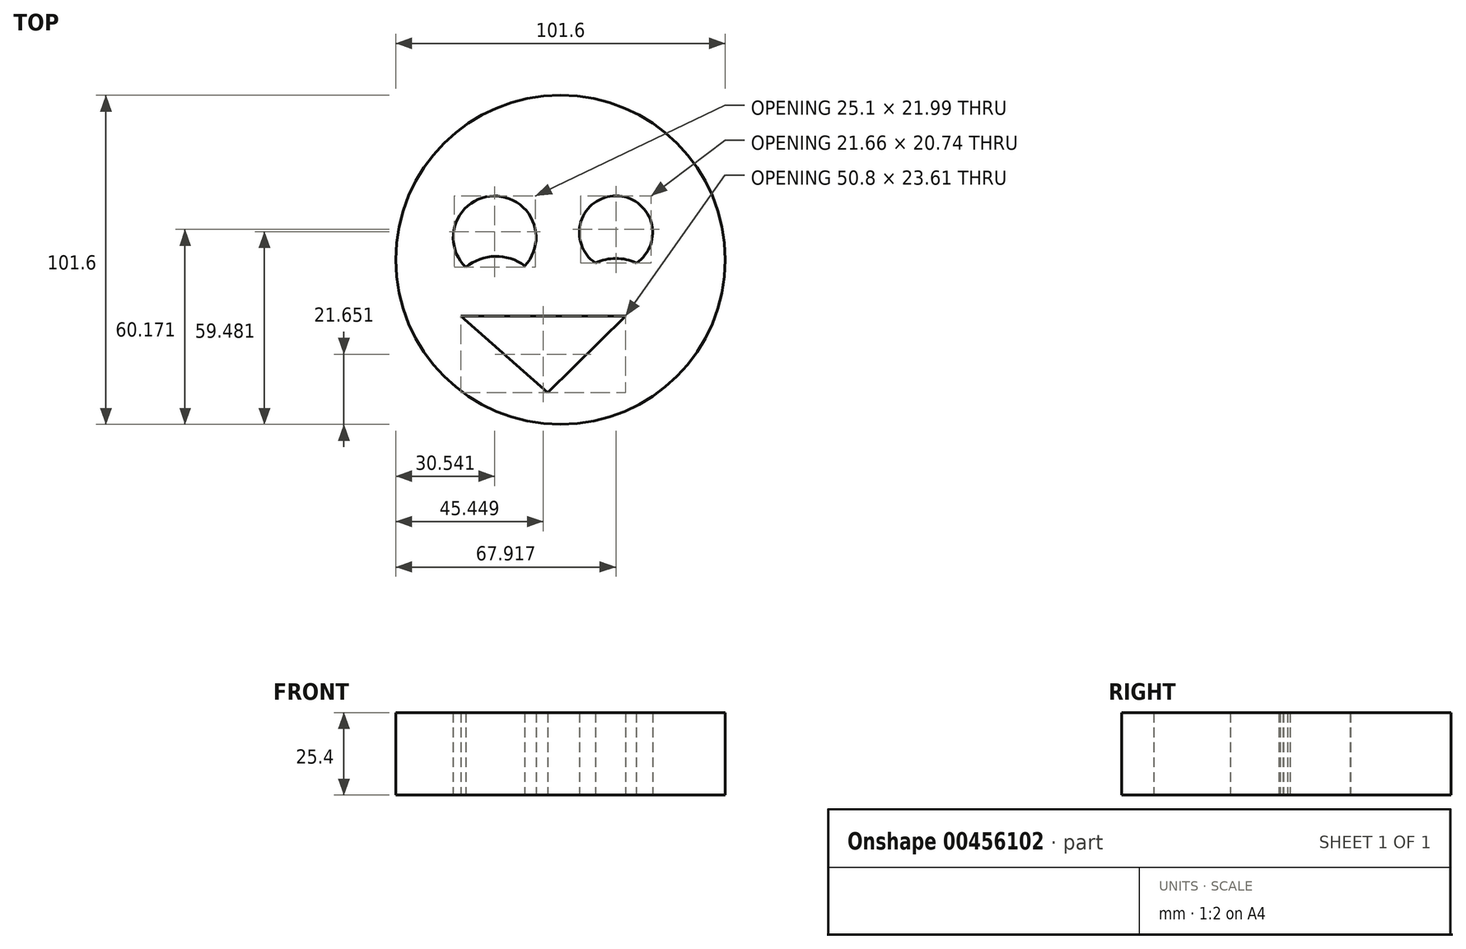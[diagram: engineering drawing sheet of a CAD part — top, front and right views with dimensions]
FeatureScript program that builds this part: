
annotation { "Feature Type Name" : "Feature", "Feature Type Description" : "" }
export const myFeature = defineFeature(function(context is Context, id is Id, definition is map)
    precondition{}
    {
        {
            var Q0;
            Q0=qCreatedBy(makeId("Top.planeOp"),FACE);
            var sketch = newSketch(context, id + "F0", { "sketchPlane" : qUnion([Q0])});
            skCircle(sketch, "E0", {"center": v(0, 0) * mm, "radius": 50.8 * mm});
            skLineSegment(sketch, "E1", {"start": v(-30.75, -17.34) * mm, "end": v(20.05, -17.34) * mm});
            skLineSegment(sketch, "E2", {"start": v(20.05, -17.34) * mm, "end": v(-3.93, -40.95) * mm});
            skLineSegment(sketch, "E3", {"start": v(-3.93, -40.95) * mm, "end": v(-30.75, -17.34) * mm});
            skArc(sketch, "E4", {"start": v(-8.6, -4.23) * mm, "mid": v(-20.04, 1.07) * mm, "end": v(-31.33, -4.52) * mm});
            skArc(sketch, "E5", {"start": v(26.67, -3.06) * mm, "mid": v(17.05, 0.41) * mm, "end": v(7.43, -3.06) * mm});
            skArc(sketch, "E6", {"start": v(-11.02, -1.9) * mm, "mid": v(-20.6, 19.68) * mm, "end": v(-29.2, -2.32) * mm});
            skArc(sketch, "E7", {"start": v(23.4, -1) * mm, "mid": v(17.14, 19.74) * mm, "end": v(10.76, -0.97) * mm});
            skSolve(sketch);
        }
        {
            var Q0;
            Q0=makeQuery(id+"F0.imprint","IMPRINT",FACE,{"disambiguationData":[TD([[makeQuery(id+"F0.imprint","IMPRINT",EDGE,{"derivedFrom":sQuery(id+"F0.wireOp",EDGE,"E0")}),1.0]])]});
            extrude(context, id + "F1", {"entities" : qUnion([Q0]), "depth" : 25.4 * mm});
        }
    });
